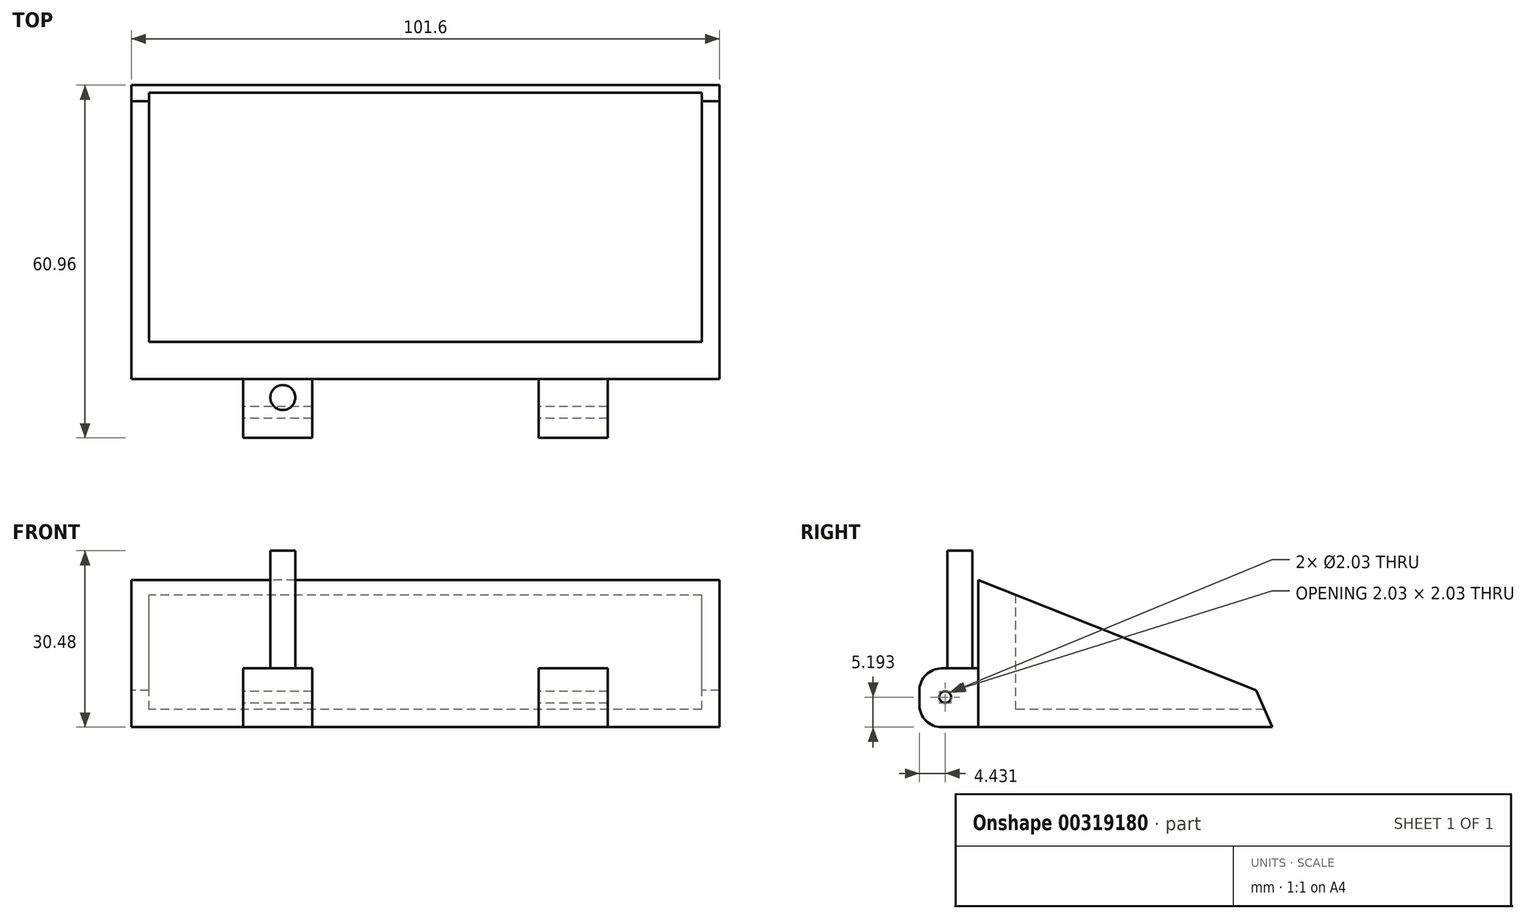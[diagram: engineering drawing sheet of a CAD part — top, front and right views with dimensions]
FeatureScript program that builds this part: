
annotation { "Feature Type Name" : "Feature", "Feature Type Description" : "" }
export const myFeature = defineFeature(function(context is Context, id is Id, definition is map)
    precondition{}
    {
        {
            var Q0;
            Q0=qCreatedBy(makeId("Right.planeOp"),FACE);
            var sketch = newSketch(context, id + "F0", { "sketchPlane" : qUnion([Q0])});
            skLineSegment(sketch, "E0", {"start": v(-35.62, 10.1) * mm, "end": v(8.8, 10.1) * mm});
            skLineSegment(sketch, "E1", {"start": v(8.8, 10.1) * mm, "end": v(6, 16.46) * mm});
            skLineSegment(sketch, "E2", {"start": v(6, 16.46) * mm, "end": v(-42, 35.5) * mm});
            skLineSegment(sketch, "E3", {"start": v(-42, 35.5) * mm, "end": v(-42, 10.1) * mm});
            skLineSegment(sketch, "E4", {"start": v(-42, 10.1) * mm, "end": v(-35.62, 10.1) * mm});
            skLineSegment(sketch, "E5.bottom", {"start": v(-42, 10.1) * mm, "end": v(-48.35, 10.1) * mm});
            skLineSegment(sketch, "E5.top", {"start": v(-42, 20.26) * mm, "end": v(-48.35, 20.26) * mm});
            skLineSegment(sketch, "E5.left", {"start": v(-42, 10.1) * mm, "end": v(-42, 20.26) * mm});
            skLineSegment(sketch, "E5.right", {"start": v(-52.16, 13.9) * mm, "end": v(-52.16, 16.45) * mm});
            skPoint(sketch, "E6.visualSharp", {"position": v(-52.16, 20.26) * mm});
            skArc(sketch, "E6.filletArc", {"start": v(-48.35, 20.26) * mm, "mid": v(-51.05, 19.14) * mm, "end": v(-52.16, 16.45) * mm});
            skPoint(sketch, "E7.visualSharp", {"position": v(-52.16, 10.1) * mm});
            skArc(sketch, "E7.filletArc", {"start": v(-52.16, 13.9) * mm, "mid": v(-51.05, 11.22) * mm, "end": v(-48.35, 10.1) * mm});
            skCircle(sketch, "E8", {"center": v(-47.73, 15.3) * mm, "radius": 1.02 * mm});
            skSolve(sketch);
        }
        {
            var Q0;
            Q0=makeQuery(id+"F0.imprint","IMPRINT",FACE,{"disambiguationData":[TD([[makeQuery(id+"F0.imprint","IMPRINT",EDGE,{"derivedFrom":sQuery(id+"F0.wireOp",EDGE,"E0")}),1.0]])]});
            extrude(context, id + "F1", {"entities" : qUnion([Q0]), "endBound" : BoundingType.SYMMETRIC, "depth" : 101.6 * mm});
        }
        {
            var Q0;
            Q0=makeQuery(id+"F0.imprint","IMPRINT",FACE,{"disambiguationData":[TD([[makeQuery(id+"F0.imprint","IMPRINT",EDGE,{"derivedFrom":sQuery(id+"F0.wireOp",EDGE,"E5.bottom")}),-1.0]])]});
            extrude(context, id + "F2", {"entities" : qUnion([Q0]), "operationType" : NewBodyOperationType.ADD, "endBound" : BoundingType.SYMMETRIC, "depth" : 63 * mm});
        }
        {
            var Q0;
            Q0=makeQuery(id+"F2.opExtrude","SWEPT_FACE",FACE,{"disambiguationData":[OSD([sQuery(id+"F0.wireOp",EDGE,"E5.top")])]});
            var sketch = newSketch(context, id + "F3", { "sketchPlane" : qUnion([Q0])});
            skCircle(sketch, "E9", {"center": v(-24.64, -45.18) * mm, "radius": 2.16 * mm});
            skCircle(sketch, "E10", {"center": v(24.64, -45.18) * mm, "radius": 2.16 * mm});
            skPoint(sketch, "E11", {"position": v(31.5, -45.18) * mm});
            skPoint(sketch, "E12", {"position": v(-31.5, -45.18) * mm});
            skLineSegment(sketch, "E13.bottom", {"start": v(-19.56, -42) * mm, "end": v(19.56, -42) * mm});
            skLineSegment(sketch, "E13.top", {"start": v(-19.56, -57.79) * mm, "end": v(19.56, -57.79) * mm});
            skLineSegment(sketch, "E13.left", {"start": v(-19.56, -42) * mm, "end": v(-19.56, -57.79) * mm});
            skLineSegment(sketch, "E13.right", {"start": v(19.56, -42) * mm, "end": v(19.56, -57.79) * mm});
            skSolve(sketch);
        }
        {
            var Q0;
            Q0=makeQuery(id+"F3.imprint","IMPRINT",FACE,{"disambiguationData":[TD([[makeQuery(id+"F3.imprint","IMPRINT",EDGE,{"derivedFrom":sQuery(id+"F3.wireOp",EDGE,"E9")}),1.0]])]});
            extrude(context, id + "F4", {"entities" : qUnion([Q0]), "operationType" : NewBodyOperationType.ADD, "depth" : 20.32 * mm});
        }
        {
            var Q0;
            {var subQ0=sQuery(id+"F3.wireOp",EDGE,"E13.bottom");Q0=makeQuery(id+"F3.imprint","IMPRINT",FACE,{"disambiguationData":[TD([[makeQuery(id+"F3.imprint","IMPRINT",EDGE,{"derivedFrom":subQ0}),1.0]])]});}
            var Q1;
            {var subQ0=sQuery(id+"F3.wireOp",EDGE,"E13.top");Q1=makeQuery(id+"F3.imprint","IMPRINT",FACE,{"disambiguationData":[TD([[makeQuery(id+"F3.imprint","IMPRINT",EDGE,{"derivedFrom":subQ0}),1.0]])]});}
            extrude(context, id + "F5", {"entities" : qUnion([Q0, Q1]), "operationType" : NewBodyOperationType.REMOVE, "oppositeDirection" : true, "depth" : 25.4 * mm});
        }
        {
            var Q0;
            Q0=qCreatedBy(makeId("Front.planeOp"),FACE);
            var sketch = newSketch(context, id + "F6", { "sketchPlane" : qUnion([Q0])});
            skLineSegment(sketch, "E14.bottom", {"start": v(47.75, 13.15) * mm, "end": v(-47.75, 13.15) * mm});
            skLineSegment(sketch, "E14.top", {"start": v(47.75, 41.03) * mm, "end": v(-47.75, 41.03) * mm});
            skLineSegment(sketch, "E14.left", {"start": v(47.75, 13.15) * mm, "end": v(47.75, 41.03) * mm});
            skLineSegment(sketch, "E14.right", {"start": v(-47.75, 13.15) * mm, "end": v(-47.75, 41.03) * mm});
            skPoint(sketch, "E14.middle", {"position": v(0, 27.1) * mm});
            skSolve(sketch);
        }
        {
            var Q0;
            Q0=makeQuery(id+"F6.imprint","IMPRINT",FACE,{"disambiguationData":[TD([[makeQuery(id+"F6.imprint","IMPRINT",EDGE,{"derivedFrom":sQuery(id+"F6.wireOp",EDGE,"E14.bottom")}),-1.0]])]});
            extrude(context, id + "F7", {"entities" : qUnion([Q0]), "operationType" : NewBodyOperationType.REMOVE, "endBound" : BoundingType.SYMMETRIC, "oppositeDirection" : true, "depth" : 71.12 * mm});
        }
    });
